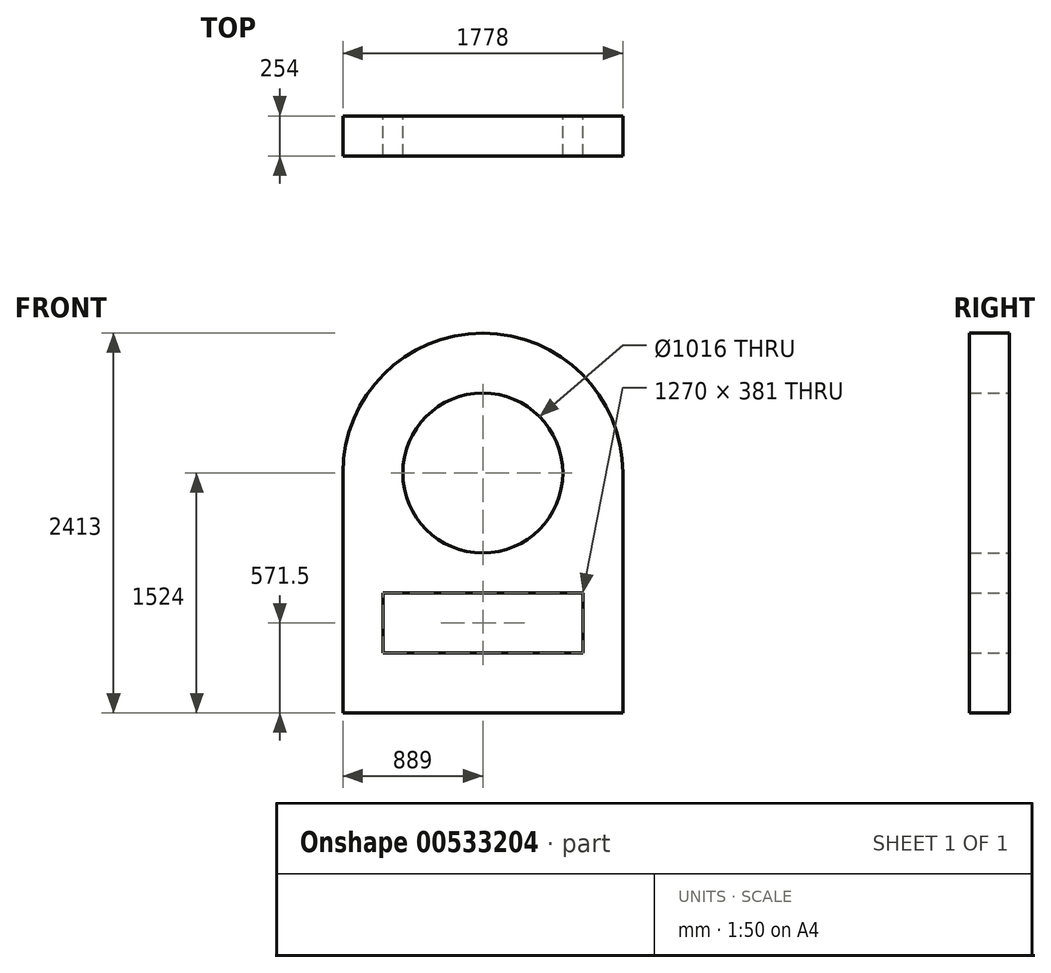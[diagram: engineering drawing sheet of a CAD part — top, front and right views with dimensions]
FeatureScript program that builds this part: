
annotation { "Feature Type Name" : "Feature", "Feature Type Description" : "" }
export const myFeature = defineFeature(function(context is Context, id is Id, definition is map)
    precondition{}
    {
        {
            var Q0;
            Q0=qCreatedBy(makeId("Front.planeOp"),FACE);
            var sketch = newSketch(context, id + "F0", { "sketchPlane" : qUnion([Q0])});
            skLineSegment(sketch, "E0", {"start": v(0, 0) * mm, "end": v(1778, 0) * mm});
            skLineSegment(sketch, "E1", {"start": v(0, 0) * mm, "end": v(0, 1524) * mm});
            skLineSegment(sketch, "E2", {"start": v(1778, 0) * mm, "end": v(1778, 1524) * mm});
            skArc(sketch, "E3", {"start": v(1778, 1524) * mm, "mid": v(889, 2413) * mm, "end": v(0, 1524) * mm});
            skCircle(sketch, "E4", {"center": v(889, 1524) * mm, "radius": 508 * mm});
            skLineSegment(sketch, "E5", {"start": v(254, 762) * mm, "end": v(1524, 762) * mm});
            skLineSegment(sketch, "E6", {"start": v(254, 762) * mm, "end": v(254, 381) * mm});
            skLineSegment(sketch, "E7", {"start": v(254, 381) * mm, "end": v(1524, 381) * mm});
            skLineSegment(sketch, "E8", {"start": v(1524, 381) * mm, "end": v(1524, 762) * mm});
            skSolve(sketch);
        }
        {
            var Q0;
            Q0 = qSketchRegion(id + "F0", true);
            extrude(context, id + "F1", {"entities" : qUnion([Q0]), "depth" : 254 * mm, "offsetDistance" : 25.4 * mm});
        }
    });
